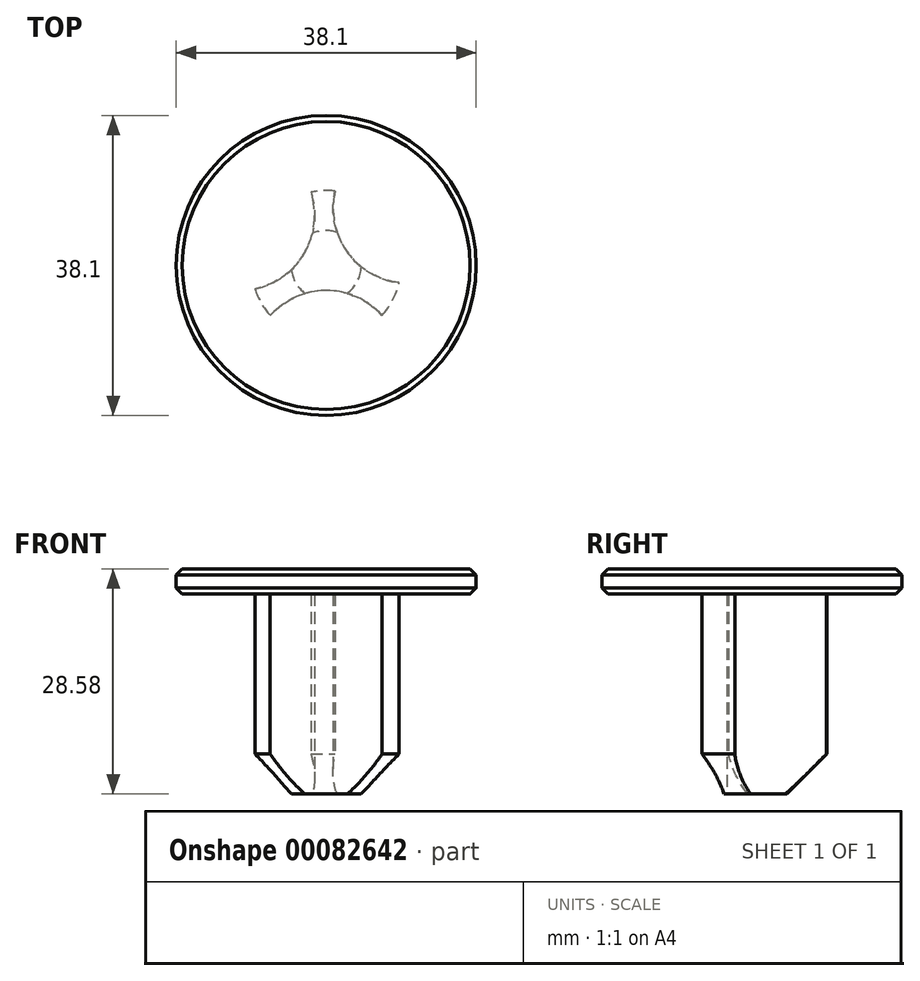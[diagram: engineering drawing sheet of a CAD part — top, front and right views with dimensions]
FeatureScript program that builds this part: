
annotation { "Feature Type Name" : "Feature", "Feature Type Description" : "" }
export const myFeature = defineFeature(function(context is Context, id is Id, definition is map)
    precondition{}
    {
        {
            var Q0;
            Q0=qCreatedBy(makeId("Front.planeOp"),FACE);
            var sketch = newSketch(context, id + "F0", { "sketchPlane" : qUnion([Q0])});
            skLineSegment(sketch, "E0.bottom", {"start": v(0, 0) * mm, "end": v(-19.05, 0) * mm});
            skLineSegment(sketch, "E0.top", {"start": v(0, 3.18) * mm, "end": v(-19.05, 3.18) * mm});
            skLineSegment(sketch, "E0.left", {"start": v(0, 0) * mm, "end": v(0, 3.18) * mm});
            skLineSegment(sketch, "E0.right", {"start": v(-19.05, 0) * mm, "end": v(-19.05, 3.18) * mm});
            skLineSegment(sketch, "E1.bottom", {"start": v(-9.53, 0) * mm, "end": v(0, 0) * mm});
            skLineSegment(sketch, "E1.top", {"start": v(-9.52, -25.4) * mm, "end": v(0, -25.4) * mm});
            skLineSegment(sketch, "E1.left", {"start": v(-9.53, 0) * mm, "end": v(-9.52, -25.4) * mm});
            skLineSegment(sketch, "E1.right", {"start": v(0, 0) * mm, "end": v(0, -25.4) * mm});
            skSolve(sketch);
        }
        {
            var Q0;
            Q0 = qSketchRegion(id + "F0", true);
            var Q1;
            Q1=sQuery(id+"F0.wireOp",EDGE,"E1.right");
            revolve(context, id + "F1", {"entities" : qUnion([Q0]), "axis" : qUnion([Q1]), "revolveType" : RevolveType.FULL});
        }
        {
            var Q0;
            Q0=makeQuery(id+"F1.opRevolve","SWEPT_EDGE",EDGE,{"disambiguationData":[OSD([sQuery(id+"F0.wireOp",EDGE,"E0.bottom"),sQuery(id+"F0.wireOp",EDGE,"E0.right")])]});
            var Q1;
            Q1=makeQuery(id+"F1.opRevolve","SWEPT_EDGE",EDGE,{"disambiguationData":[OSD([sQuery(id+"F0.wireOp",EDGE,"E0.top"),sQuery(id+"F0.wireOp",EDGE,"E0.right")])]});
            chamfer(context, id + "F2", {"entities" : qUnion([Q0, Q1]), "width" : 0.76 * mm, "tangentPropagation" : true});
        }
        {
            var Q0;
            Q0=makeQuery(id+"F1.opRevolve","SWEPT_FACE",FACE,{"disambiguationData":[OSD([sQuery(id+"F0.wireOp",EDGE,"E1.top")])]});
            var sketch = newSketch(context, id + "F3", { "sketchPlane" : qUnion([Q0])});
            skPoint(sketch, "E2.0.midPoint", {"position": v(5.5, 3.18) * mm});
            skCircle(sketch, "E3", {"center": v(0, 12.7) * mm, "radius": 9.53 * mm});
            skCircle(sketch, "E4", {"center": v(-11, -6.35) * mm, "radius": 9.53 * mm});
            skPoint(sketch, "E5", {"position": v(10.4, -7.28) * mm});
            skCircle(sketch, "E6", {"center": v(10.4, -7.28) * mm, "radius": 9.53 * mm});
            skSolve(sketch);
        }
        {
            var Q0;
            Q0 = qSketchRegion(id + "F3", true);
            var Q1;
            Q1=makeQuery(id+"F1.opRevolve","SWEPT_FACE",FACE,{"disambiguationData":[OSD([sQuery(id+"F0.wireOp",EDGE,"E0.bottom")])]});
            extrude(context, id + "F4", {"entities" : qUnion([Q0]), "operationType" : NewBodyOperationType.REMOVE, "endBound" : BoundingType.UP_TO_SURFACE, "oppositeDirection" : true, "endBoundEntityFace" : qUnion([Q1]), "depth" : 25.4 * mm});
        }
        {
            var Q0;
            {var subQ0=sQuery(id+"F0.wireOp",EDGE,"E1.top");var subQ1=makeQuery(id+"F1.opRevolve","SWEPT_FACE",FACE,{"disambiguationData":[OSD([subQ0])]});var subQ2=sQuery(id+"F0.wireOp",EDGE,"E1.left");var subQ3=makeQuery(id+"F1.opRevolve","SWEPT_FACE",FACE,{"disambiguationData":[OSD([subQ2])]});var subQ4=makeQuery(id+"F4.opExtrude","SWEPT_FACE",FACE,{"disambiguationData":[OSD([sQuery(id+"F3.wireOp",EDGE,"E4")])]});var subQ5=makeQuery(id+"F1.opRevolve","SWEPT_EDGE",EDGE,{"disambiguationData":[OSD([subQ0,subQ2])]});Q0=qUnion([makeQuery(id+"F4.boolean.opBoolean","SPLIT",EDGE,{"disambiguationData":[TD([subQ1,subQ3,makeQuery(id+"F4.opExtrude","SWEPT_FACE",FACE,{"disambiguationData":[OSD([sQuery(id+"F3.wireOp",EDGE,"E3")])]}),subQ4])],"derivedFrom":subQ5}),makeQuery(id+"F4.boolean.opBoolean","SPLIT",EDGE,{"disambiguationData":[TD([subQ1,subQ3,subQ4,makeQuery(id+"F4.opExtrude","SWEPT_FACE",FACE,{"disambiguationData":[OSD([sQuery(id+"F3.wireOp",EDGE,"E6")])]})])],"derivedFrom":subQ5})]);}
            var Q1;
            {var subQ0=sQuery(id+"F0.wireOp",EDGE,"E1.top");var subQ1=makeQuery(id+"F1.opRevolve","SWEPT_FACE",FACE,{"disambiguationData":[OSD([subQ0])]});var subQ2=sQuery(id+"F0.wireOp",EDGE,"E1.left");var subQ3=makeQuery(id+"F1.opRevolve","SWEPT_FACE",FACE,{"disambiguationData":[OSD([subQ2])]});var subQ4=makeQuery(id+"F4.opExtrude","SWEPT_FACE",FACE,{"disambiguationData":[OSD([sQuery(id+"F3.wireOp",EDGE,"E3")])]});var subQ5=makeQuery(id+"F1.opRevolve","SWEPT_EDGE",EDGE,{"disambiguationData":[OSD([subQ0,subQ2])]});Q1=qUnion([makeQuery(id+"F4.boolean.opBoolean","SPLIT",EDGE,{"disambiguationData":[TD([subQ1,subQ3,subQ4,makeQuery(id+"F4.opExtrude","SWEPT_FACE",FACE,{"disambiguationData":[OSD([sQuery(id+"F3.wireOp",EDGE,"E4")])]})])],"derivedFrom":subQ5}),makeQuery(id+"F4.boolean.opBoolean","SPLIT",EDGE,{"disambiguationData":[TD([subQ1,subQ3,subQ4,makeQuery(id+"F4.opExtrude","SWEPT_FACE",FACE,{"disambiguationData":[OSD([sQuery(id+"F3.wireOp",EDGE,"E6")])]})])],"derivedFrom":subQ5})]);}
            var Q2;
            {var subQ0=sQuery(id+"F0.wireOp",EDGE,"E1.top");var subQ1=sQuery(id+"F0.wireOp",EDGE,"E1.left");Q2=makeQuery(id+"F4.boolean.opBoolean","SPLIT",EDGE,{"disambiguationData":[TD([makeQuery(id+"F1.opRevolve","SWEPT_FACE",FACE,{"disambiguationData":[OSD([subQ0])]}),makeQuery(id+"F1.opRevolve","SWEPT_FACE",FACE,{"disambiguationData":[OSD([subQ1])]}),makeQuery(id+"F4.opExtrude","SWEPT_FACE",FACE,{"disambiguationData":[OSD([sQuery(id+"F3.wireOp",EDGE,"E3")])]}),makeQuery(id+"F4.opExtrude","SWEPT_FACE",FACE,{"disambiguationData":[OSD([sQuery(id+"F3.wireOp",EDGE,"E4")])]})])],"derivedFrom":makeQuery(id+"F1.opRevolve","SWEPT_EDGE",EDGE,{"disambiguationData":[OSD([subQ0,subQ1])]})});}
            chamfer(context, id + "F5", {"entities" : qUnion([Q0, Q1, Q2]), "width" : 5.08 * mm, "tangentPropagation" : true});
        }
    });
